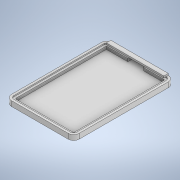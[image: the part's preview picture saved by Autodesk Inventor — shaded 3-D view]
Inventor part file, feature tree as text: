
AUTODESK INVENTOR PART (.ipt)
format: ipt  version: 2022 (Build 260153000, 153)  size: 195,072 bytes
history: native  units: in
note: dims shown in document units (in); Inventor stores cm internally (conversion verified against a paired STEP export)
features: extrude x5, sketch x5
ambient origin geometry x8: Origin, YZ Plane, XZ Plane, XY Plane, X Axis, Y Axis, Z Axis, Center Point
bodies: Solid1 (feature_tree)
feature tree (10):
  extrude  "Extrusion1"  Depth=3.3465in
  extrude  "Extrusion2"  Depth=0.1181in
  extrude  "Extrusion3"  Depth=0.0394in TaperAngle=0.0deg
  extrude  "Extrusion4"  Depth=0.0591in
  extrude  "Extrusion5"  Depth=0.1575in
  sketch  "Sketch1"  dims[d0=2.2047in d1=3.3465in]
  sketch  "Sketch2"  dims[d2=0.0787in d3=0.1181in]
  sketch  "Sketch3"  dims[d4=0.0787in d5=0.0394in d6=0.0in]
  sketch  "Sketch4"  dims[d7=0.0984in d8=0.0in d9=0.0591in]
  sketch  "Sketch5"  dims[d10=0.1575in d11=0.0in d12=0.1575in d13=0.0394in d14=0.0in d16=0.5512in d17=0.0394in d18=0.0984in d19=0.0394in d20=0.0in]
